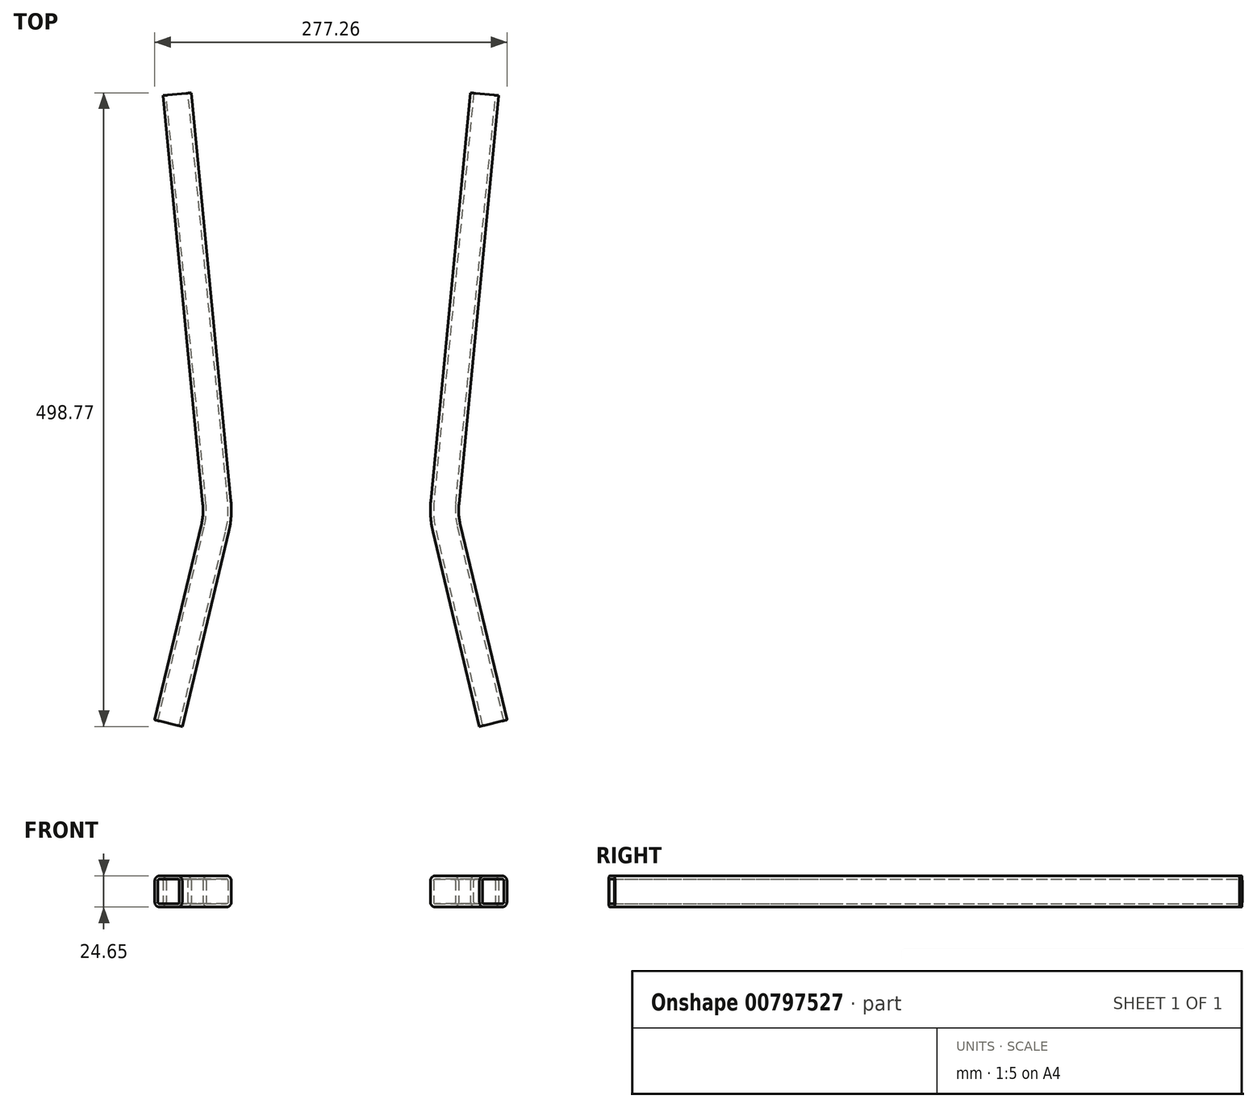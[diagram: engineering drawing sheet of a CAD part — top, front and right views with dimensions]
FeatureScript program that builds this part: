
annotation { "Feature Type Name" : "Feature", "Feature Type Description" : "" }
export const myFeature = defineFeature(function(context is Context, id is Id, definition is map)
    precondition{}
    {
        {
            var Q0;
            Q0=qCreatedBy(makeId("Top.planeOp"),FACE);
            var sketch = newSketch(context, id + "F0", { "sketchPlane" : qUnion([Q0])});
            skLineSegment(sketch, "E0", {"start": v(0, 0) * mm, "end": v(0, 382.6) * mm, "construction": true});
            skLineSegment(sketch, "E1", {"start": v(0, 0) * mm, "end": v(77.5, 0) * mm, "construction": true});
            skLineSegment(sketch, "E2", {"start": v(80.3, -11.72) * mm, "end": v(117, -165.35) * mm});
            skLineSegment(sketch, "E3", {"start": v(78.67, 12) * mm, "end": v(110, 333.42) * mm});
            skPoint(sketch, "E4.visualSharp", {"position": v(77.5, 0) * mm});
            skArc(sketch, "E4.filletArc", {"start": v(78.67, 12) * mm, "mid": v(78.5, 0.07) * mm, "end": v(80.3, -11.72) * mm});
            skSolve(sketch);
        }
        {
            var Q0;
            Q0=sQuery(id+"F0.wireOp",VERTEX,"E2.end");
            var Q1;
            Q1=sQuery(id+"F0.wireOp",EDGE,"E2");
            cPlane(context, id + "F1", {"entities" : qUnion([Q0, Q1]), "cplaneType" : CPlaneType.LINE_POINT, "offset" : 25 * mm, "width" : 150 * mm, "height" : 150 * mm});
        }
        {
            var Q0;
            Q0=qCreatedBy(id+"F1.planeOp",FACE);
            var sketch = newSketch(context, id + "F2", { "sketchPlane" : qUnion([Q0])});
            skLineSegment(sketch, "E5.bottom", {"start": v(79.38, 0) * mm, "end": v(93.61, 0) * mm});
            skLineSegment(sketch, "E5.top", {"start": v(79.38, -24.65) * mm, "end": v(93.61, -24.65) * mm});
            skLineSegment(sketch, "E5.left", {"start": v(75.38, -4) * mm, "end": v(75.38, -20.65) * mm});
            skLineSegment(sketch, "E5.right", {"start": v(97.61, -4) * mm, "end": v(97.61, -20.65) * mm});
            skPoint(sketch, "E6.visualSharp", {"position": v(75.38, 0) * mm});
            skArc(sketch, "E6.filletArc", {"start": v(79.38, 0) * mm, "mid": v(76.55, -1.17) * mm, "end": v(75.38, -4) * mm});
            skPoint(sketch, "E7.visualSharp", {"position": v(97.61, 0) * mm});
            skArc(sketch, "E7.filletArc", {"start": v(97.61, -4) * mm, "mid": v(96.44, -1.17) * mm, "end": v(93.61, 0) * mm});
            skPoint(sketch, "E8.visualSharp", {"position": v(97.61, -24.65) * mm});
            skArc(sketch, "E8.filletArc", {"start": v(93.61, -24.65) * mm, "mid": v(96.44, -23.48) * mm, "end": v(97.61, -20.65) * mm});
            skPoint(sketch, "E9.visualSharp", {"position": v(75.38, -24.65) * mm});
            skArc(sketch, "E9.filletArc", {"start": v(75.38, -20.65) * mm, "mid": v(76.55, -23.48) * mm, "end": v(79.38, -24.65) * mm});
            skSolve(sketch);
        }
        {
            var Q0;
            Q0=makeQuery(id+"F2.imprint","IMPRINT",FACE,{"disambiguationData":[TD([[makeQuery(id+"F2.imprint","IMPRINT",EDGE,{"derivedFrom":sQuery(id+"F2.wireOp",EDGE,"E5.bottom")}),-1.0]])]});
            var Q1;
            Q1 = qConstructionFilter(qBodyType(qCreatedBy(id + "F0" ,EDGE), BodyType.WIRE), ConstructionObject.NO);
            sweep(context, id + "F3", {"profiles" : qUnion([Q0]), "path" : qUnion([Q1])});
        }
        {
            var Q0;
            Q0=makeQuery(id+"F3.opSweep","CAP_FACE",FACE,{"disambiguationData":[OSD([sQuery(id+"F0.wireOp",VERTEX,"E2.end"),sQuery(id+"F2.wireOp",EDGE,"E5.bottom"),sQuery(id+"F2.wireOp",EDGE,"E5.top"),sQuery(id+"F2.wireOp",EDGE,"E5.left"),sQuery(id+"F2.wireOp",EDGE,"E5.right"),sQuery(id+"F2.wireOp",EDGE,"E6.filletArc"),sQuery(id+"F2.wireOp",EDGE,"E7.filletArc"),sQuery(id+"F2.wireOp",EDGE,"E8.filletArc"),sQuery(id+"F2.wireOp",EDGE,"E9.filletArc")])],"isStart":true});
            var Q1;
            Q1=makeQuery(id+"F3.opSweep","CAP_FACE",FACE,{"disambiguationData":[OSD([sQuery(id+"F0.wireOp",VERTEX,"E3.end"),sQuery(id+"F2.wireOp",EDGE,"E5.bottom"),sQuery(id+"F2.wireOp",EDGE,"E5.top"),sQuery(id+"F2.wireOp",EDGE,"E5.left"),sQuery(id+"F2.wireOp",EDGE,"E5.right"),sQuery(id+"F2.wireOp",EDGE,"E6.filletArc"),sQuery(id+"F2.wireOp",EDGE,"E7.filletArc"),sQuery(id+"F2.wireOp",EDGE,"E8.filletArc"),sQuery(id+"F2.wireOp",EDGE,"E9.filletArc")])],"isStart":false});
            shell(context, id + "F4", {"entities" : qUnion([Q0, Q1]), "thickness" : 2.5 * mm});
        }
        {
            var Q0;
            Q0=qCreatedBy(makeId("Top.planeOp"),FACE);
            var sketch = newSketch(context, id + "F5", { "sketchPlane" : qUnion([Q0])});
            skLineSegment(sketch, "E10.0", {"start": v(78.67, 12) * mm, "end": v(105.96, 292) * mm});
            skLineSegment(sketch, "E11", {"start": v(105.96, 292) * mm, "end": v(0, 292) * mm});
            skLineSegment(sketch, "E12", {"start": v(78.67, 12) * mm, "end": v(0, 12) * mm});
            skLineSegment(sketch, "E13", {"start": v(0, 12) * mm, "end": v(0, 292) * mm});
            skSolve(sketch);
        }
        {
            var Q0;
            Q0=qCreatedBy(makeId("Front.planeOp"),FACE);
            var Q1;
            Q1=sQuery(id+"F5.wireOp",VERTEX,"E12.end");
            cPlane(context, id + "F6", {"entities" : qUnion([Q0, Q1]), "cplaneType" : CPlaneType.PLANE_POINT, "offset" : 25 * mm, "width" : 150 * mm, "height" : 150 * mm});
        }
        {
            var Q0;
            Q0=qCreatedBy(id+"F6.planeOp",FACE);
            var sketch = newSketch(context, id + "F7", { "sketchPlane" : qUnion([Q0])});
            skLineSegment(sketch, "E14", {"start": v(78.67, 0) * mm, "end": v(42.5, -130) * mm});
            skLineSegment(sketch, "E15", {"start": v(42.5, -130) * mm, "end": v(0, -130) * mm});
            skLineSegment(sketch, "E16", {"start": v(0, -130) * mm, "end": v(0, 0) * mm});
            skLineSegment(sketch, "E17", {"start": v(0, 0) * mm, "end": v(78.67, 0) * mm});
            skSolve(sketch);
        }
        {
            var Q0;
            Q0=makeQuery(id+"F3.opSweep","SWEPT_BODY",BODY,{"disambiguationData":[OSD([sQuery(id+"F0.wireOp",EDGE,"E2"),sQuery(id+"F2.wireOp",EDGE,"E5.bottom"),sQuery(id+"F2.wireOp",EDGE,"E5.top"),sQuery(id+"F2.wireOp",EDGE,"E5.left"),sQuery(id+"F2.wireOp",EDGE,"E5.right"),sQuery(id+"F2.wireOp",EDGE,"E6.filletArc"),sQuery(id+"F2.wireOp",EDGE,"E7.filletArc"),sQuery(id+"F2.wireOp",EDGE,"E8.filletArc"),sQuery(id+"F2.wireOp",EDGE,"E9.filletArc")])]});
            var Q1;
            Q1=qCreatedBy(makeId("Right.planeOp"),FACE);
            mirror(context, id + "F8", {"entities" : qUnion([Q0]), "mirrorPlane" : qUnion([Q1])});
        }
        {
            var Q0;
            Q0=qCreatedBy(makeId("Right.planeOp"),FACE);
            var sketch = newSketch(context, id + "F9", { "sketchPlane" : qUnion([Q0])});
            skLineSegment(sketch, "E18", {"start": v(12, -130) * mm, "end": v(212, -130) * mm});
            skLineSegment(sketch, "E19", {"start": v(212, -130) * mm, "end": v(292, 0) * mm});
            skLineSegment(sketch, "E20.0", {"start": v(12, -130) * mm, "end": v(12, 0) * mm});
            skLineSegment(sketch, "E21.0", {"start": v(12, 0) * mm, "end": v(292, 0) * mm});
            skSolve(sketch);
        }
        {
            var Q0;
            Q0=sQuery(id+"F5.wireOp",VERTEX,"E11.end");
            var Q1;
            Q1=sQuery(id+"F5.wireOp",VERTEX,"E10.0.end");
            var Q2;
            Q2=sQuery(id+"F9.wireOp",VERTEX,"E18.end");
            cPlane(context, id + "F10", {"entities" : qUnion([Q0, Q1, Q2]), "cplaneType" : CPlaneType.THREE_POINT, "offset" : 25 * mm, "width" : 150 * mm, "height" : 150 * mm});
        }
    });
